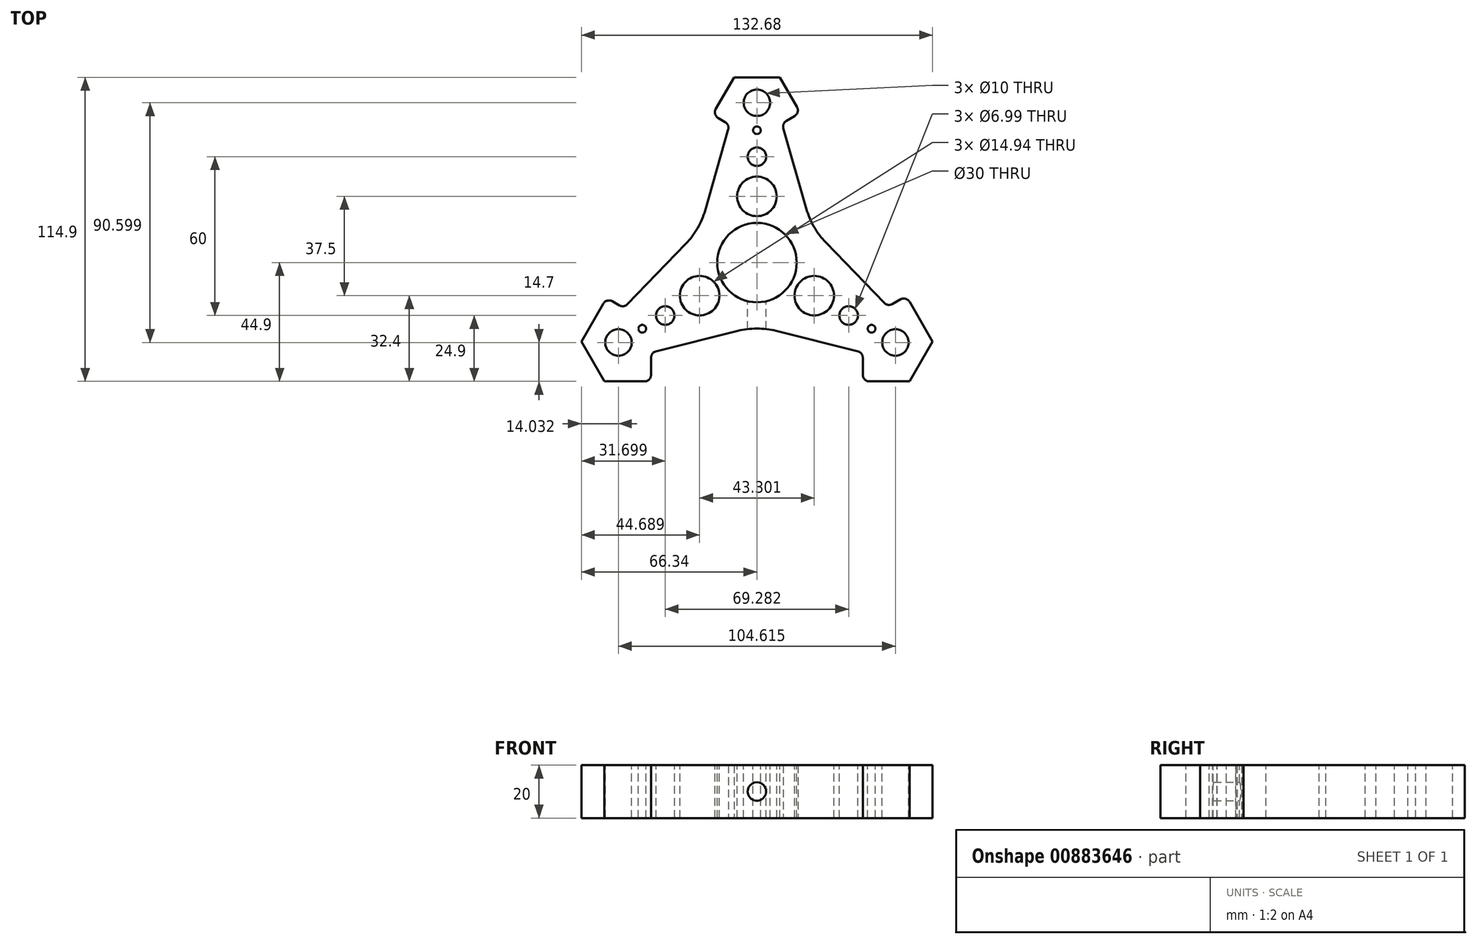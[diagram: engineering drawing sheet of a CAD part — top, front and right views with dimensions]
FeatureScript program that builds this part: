
annotation { "Feature Type Name" : "Feature", "Feature Type Description" : "" }
export const myFeature = defineFeature(function(context is Context, id is Id, definition is map)
    precondition{}
    {
        {
            var Q0;
            Q0=qCreatedBy(makeId("Top.planeOp"),FACE);
            var sketch = newSketch(context, id + "F0", { "sketchPlane" : qUnion([Q0])});
            skLineSegment(sketch, "E0", {"start": v(0, 0) * mm, "end": v(0, 85) * mm});
            skLineSegment(sketch, "E1", {"start": v(0, 85) * mm, "end": v(75, -44.9) * mm});
            skLineSegment(sketch, "E2", {"start": v(75, -44.9) * mm, "end": v(-75, -44.9) * mm});
            skLineSegment(sketch, "E3", {"start": v(-75, -44.9) * mm, "end": v(0, 85) * mm});
            skSolve(sketch);
        }
        {
            var Q0;
            Q0=makeQuery(id+"F0.imprint","IMPRINT",FACE,{"disambiguationData":[TD([[makeQuery(id+"F0.imprint","IMPRINT",EDGE,{"derivedFrom":sQuery(id+"F0.wireOp",EDGE,"E1")}),-1.0]])]});
            extrude(context, id + "F1", {"entities" : qUnion([Q0]), "depth" : 20 * mm, "offsetDistance" : 25 * mm});
        }
        {
            var Q0;
            Q0=makeQuery(id+"F1.opExtrude","SWEPT_EDGE",EDGE,{"disambiguationData":[OSD([sQuery(id+"F0.wireOp",EDGE,"E2"),sQuery(id+"F0.wireOp",EDGE,"E3")])]});
            var Q1;
            Q1=makeQuery(id+"F1.opExtrude","SWEPT_EDGE",EDGE,{"disambiguationData":[OSD([sQuery(id+"F0.wireOp",EDGE,"E1"),sQuery(id+"F0.wireOp",EDGE,"E2")])]});
            var Q2;
            Q2=makeQuery(id+"F1.opExtrude","SWEPT_EDGE",EDGE,{"disambiguationData":[OSD([sQuery(id+"F0.wireOp",EDGE,"E1"),sQuery(id+"F0.wireOp",EDGE,"E3")])]});
            chamfer(context, id + "F2", {"entities" : qUnion([Q0, Q1, Q2]), "width" : 10 * mm, "tangentPropagation" : true});
        }
        {
            var Q0;
            Q0=makeQuery(id+"F1.opExtrude","CAP_FACE",FACE,{"disambiguationData":[OSD([sQuery(id+"F0.wireOp",EDGE,"E1"),sQuery(id+"F0.wireOp",EDGE,"E2"),sQuery(id+"F0.wireOp",EDGE,"E3")])],"isStart":false});
            var sketch = newSketch(context, id + "F3", { "sketchPlane" : qUnion([Q0])});
            skCircle(sketch, "E4", {"center": v(0, 60.4) * mm, "radius": 3.81 * mm});
            skCircle(sketch, "E5.1.0", {"center": v(-52.3, -30.2) * mm, "radius": 3.81 * mm});
            skCircle(sketch, "E5.2.0", {"center": v(52.3, -30.2) * mm, "radius": 3.81 * mm});
            skPoint(sketch, "E5.center", {"position": v(0, 0) * mm});
            skSolve(sketch);
        }
        {
            var Q0;
            Q0=sQuery(id+"F3.wireOp",VERTEX,"E4.center");
            var Q1;
            Q1=sQuery(id+"F3.wireOp",VERTEX,"E5.2.0.center");
            var Q2;
            Q2=sQuery(id+"F3.wireOp",VERTEX,"E5.1.0.center");
            var Q3;
            Q3=makeQuery(id+"F1.opExtrude","SWEPT_BODY",BODY,{"disambiguationData":[OSD([sQuery(id+"F0.wireOp",EDGE,"E1"),sQuery(id+"F0.wireOp",EDGE,"E2"),sQuery(id+"F0.wireOp",EDGE,"E3")])]});
            hole(context, id + "F4", {"style" : HoleStyle.SIMPLE, "endStyle" : HoleEndStyle.BLIND, "holeDiameter" : 10 * mm, "majorDiameter" : 5 * mm, "holeDepth" : 100 * mm, "isTappedThrough" : true, "tappedDepth" : 12 * mm, "tapClearance" : 3, "locations" : qUnion([Q0, Q1, Q2]), "scope" : qUnion([Q3])});
        }
        {
            var Q0;
            Q0=makeQuery(id+"F1.opExtrude","CAP_FACE",FACE,{"disambiguationData":[OSD([sQuery(id+"F0.wireOp",EDGE,"E1"),sQuery(id+"F0.wireOp",EDGE,"E2"),sQuery(id+"F0.wireOp",EDGE,"E3")])],"isStart":false});
            var sketch = newSketch(context, id + "F5", { "sketchPlane" : qUnion([Q0])});
            skSolve(sketch);
        }
        {
            var Q0;
            {var subQ0=sQuery(id+"F0.wireOp",EDGE,"E1");Q0=makeQuery(id+"F5.imprint","IMPRINT",FACE,{"disambiguationData":[TD([[makeQuery(id+"F5.imprint","IMPRINT",EDGE,{"derivedFrom":makeQuery(id+"F1.opExtrude","CAP_EDGE",EDGE,{"disambiguationData":[OSD([subQ0])],"isStart":false})}),-1.0]])]});}
            var sketch = newSketch(context, id + "F6", { "sketchPlane" : qUnion([Q0])});
            skCircle(sketch, "E6", {"center": v(0, 0) * mm, "radius": 12.1 * mm});
            skSolve(sketch);
        }
        {
            var Q0;
            Q0=sQuery(id+"F6.wireOp",VERTEX,"E6.center");
            var Q1;
            Q1=makeQuery(id+"F1.opExtrude","SWEPT_BODY",BODY,{"disambiguationData":[OSD([sQuery(id+"F0.wireOp",EDGE,"E1"),sQuery(id+"F0.wireOp",EDGE,"E2"),sQuery(id+"F0.wireOp",EDGE,"E3")])]});
            hole(context, id + "F7", {"style" : HoleStyle.SIMPLE, "endStyle" : HoleEndStyle.BLIND, "holeDiameter" : 30 * mm, "majorDiameter" : 5 * mm, "holeDepth" : 100 * mm, "isTappedThrough" : true, "tappedDepth" : 12 * mm, "tapClearance" : 3, "locations" : qUnion([Q0]), "scope" : qUnion([Q1])});
        }
        {
            var Q0;
            {var subQ0=sQuery(id+"F0.wireOp",EDGE,"E1");Q0=makeQuery(id+"F5.imprint","IMPRINT",FACE,{"disambiguationData":[TD([[makeQuery(id+"F5.imprint","IMPRINT",EDGE,{"derivedFrom":makeQuery(id+"F1.opExtrude","CAP_EDGE",EDGE,{"disambiguationData":[OSD([subQ0])],"isStart":false})}),-1.0]])]});}
            var sketch = newSketch(context, id + "F8", { "sketchPlane" : qUnion([Q0])});
            skLineSegment(sketch, "E7", {"start": v(0, 0) * mm, "end": v(0, -48) * mm});
            skLineSegment(sketch, "E8", {"start": v(0, -48) * mm, "end": v(40, -48) * mm});
            skLineSegment(sketch, "E9", {"start": v(40, -48) * mm, "end": v(40, -34) * mm});
            skLineSegment(sketch, "E10", {"start": v(40, -34) * mm, "end": v(0, -24) * mm});
            skLineSegment(sketch, "E11", {"start": v(0, -24) * mm, "end": v(0, -48) * mm});
            skLineSegment(sketch, "E12.MirrorCS", {"start": v(-40, -34) * mm, "end": v(0, -24) * mm});
            skLineSegment(sketch, "E13.MirrorCS", {"start": v(-40, -48) * mm, "end": v(-40, -34) * mm});
            skLineSegment(sketch, "E14.MirrorCS", {"start": v(0, -48) * mm, "end": v(-40, -48) * mm});
            skLineSegment(sketch, "E15.1.0", {"start": v(61.57, -9.64) * mm, "end": v(49.44, -16.64) * mm});
            skLineSegment(sketch, "E15.1.1", {"start": v(20.78, 13) * mm, "end": v(41.57, 25) * mm});
            skLineSegment(sketch, "E15.1.2", {"start": v(41.57, 25) * mm, "end": v(61.57, -9.64) * mm});
            skLineSegment(sketch, "E15.1.3", {"start": v(41.57, 25) * mm, "end": v(21.57, 59.64) * mm});
            skLineSegment(sketch, "E15.1.4", {"start": v(49.44, -16.64) * mm, "end": v(20.78, 13) * mm});
            skLineSegment(sketch, "E15.1.5", {"start": v(9.44, 52.64) * mm, "end": v(20.78, 13) * mm});
            skLineSegment(sketch, "E15.1.6", {"start": v(21.57, 59.64) * mm, "end": v(9.44, 52.64) * mm});
            skLineSegment(sketch, "E15.2.0", {"start": v(-22.44, 59.14) * mm, "end": v(-10.31, 52.14) * mm});
            skLineSegment(sketch, "E15.2.1", {"start": v(-21.65, 12.5) * mm, "end": v(-42.44, 24.5) * mm});
            skLineSegment(sketch, "E15.2.2", {"start": v(-42.44, 24.5) * mm, "end": v(-22.44, 59.14) * mm});
            skLineSegment(sketch, "E15.2.3", {"start": v(-42.44, 24.5) * mm, "end": v(-62.44, -10.14) * mm});
            skLineSegment(sketch, "E15.2.4", {"start": v(-10.31, 52.14) * mm, "end": v(-21.65, 12.5) * mm});
            skLineSegment(sketch, "E15.2.5", {"start": v(-50.31, -17.14) * mm, "end": v(-21.65, 12.5) * mm});
            skLineSegment(sketch, "E15.2.6", {"start": v(-62.44, -10.14) * mm, "end": v(-50.31, -17.14) * mm});
            skPoint(sketch, "E15.center", {"position": v(-0.29, 0.5) * mm});
            skSolve(sketch);
        }
        {
            var Q0;
            Q0 = qSketchRegion(id + "F8", true);
            extrude(context, id + "F9", {"entities" : qUnion([Q0]), "operationType" : NewBodyOperationType.REMOVE, "oppositeDirection" : true, "depth" : 25 * mm, "offsetDistance" : 25 * mm});
        }
        {
            var Q0;
            Q0=makeQuery(id+"F9.boolean.opBoolean","COPY",EDGE,{"derivedFrom":makeQuery(id+"F9.opExtrude","SWEPT_EDGE",EDGE,{"disambiguationData":[OSD([sQuery(id+"F8.wireOp",EDGE,"E12.MirrorCS"),sQuery(id+"F8.wireOp",EDGE,"E13.MirrorCS")])]})});
            var Q1;
            Q1=makeQuery(id+"F9.boolean.opBoolean","COPY",EDGE,{"derivedFrom":makeQuery(id+"F9.opExtrude","SWEPT_EDGE",EDGE,{"disambiguationData":[OSD([sQuery(id+"F8.wireOp",EDGE,"E15.2.5"),sQuery(id+"F8.wireOp",EDGE,"E15.2.6")])]})});
            var Q2;
            Q2=makeQuery(id+"F9.boolean.opBoolean","COPY",EDGE,{"derivedFrom":makeQuery(id+"F9.opExtrude","SWEPT_EDGE",EDGE,{"disambiguationData":[OSD([sQuery(id+"F8.wireOp",EDGE,"E15.2.0"),sQuery(id+"F8.wireOp",EDGE,"E15.2.4")])]})});
            var Q3;
            Q3=makeQuery(id+"F9.boolean.opBoolean","COPY",EDGE,{"derivedFrom":makeQuery(id+"F9.opExtrude","SWEPT_EDGE",EDGE,{"disambiguationData":[OSD([sQuery(id+"F8.wireOp",EDGE,"E15.1.5"),sQuery(id+"F8.wireOp",EDGE,"E15.1.6")])]})});
            var Q4;
            Q4=makeQuery(id+"F9.boolean.opBoolean","COPY",EDGE,{"derivedFrom":makeQuery(id+"F9.opExtrude","SWEPT_EDGE",EDGE,{"disambiguationData":[OSD([sQuery(id+"F8.wireOp",EDGE,"E15.1.0"),sQuery(id+"F8.wireOp",EDGE,"E15.1.4")])]})});
            var Q5;
            Q5=makeQuery(id+"F9.boolean.opBoolean","COPY",EDGE,{"derivedFrom":makeQuery(id+"F9.opExtrude","SWEPT_EDGE",EDGE,{"disambiguationData":[OSD([sQuery(id+"F8.wireOp",EDGE,"E9"),sQuery(id+"F8.wireOp",EDGE,"E10")])]})});
            var Q6;
            Q6=makeQuery(id+"F9.boolean.opBoolean","INTERSECT",EDGE,{"derivedFrom":[makeQuery(id+"F1.opExtrude","SWEPT_FACE",FACE,{"disambiguationData":[OSD([sQuery(id+"F0.wireOp",EDGE,"E2")])]}),makeQuery(id+"F9.opExtrude","SWEPT_FACE",FACE,{"disambiguationData":[OSD([sQuery(id+"F8.wireOp",EDGE,"E9")])]})]});
            var Q7;
            Q7=makeQuery(id+"F9.boolean.opBoolean","INTERSECT",EDGE,{"derivedFrom":[makeQuery(id+"F1.opExtrude","SWEPT_FACE",FACE,{"disambiguationData":[OSD([sQuery(id+"F0.wireOp",EDGE,"E1")])]}),makeQuery(id+"F9.opExtrude","SWEPT_FACE",FACE,{"disambiguationData":[OSD([sQuery(id+"F8.wireOp",EDGE,"E15.1.0")])]})]});
            var Q8;
            Q8=makeQuery(id+"F9.boolean.opBoolean","INTERSECT",EDGE,{"derivedFrom":[makeQuery(id+"F1.opExtrude","SWEPT_FACE",FACE,{"disambiguationData":[OSD([sQuery(id+"F0.wireOp",EDGE,"E1")])]}),makeQuery(id+"F9.opExtrude","SWEPT_FACE",FACE,{"disambiguationData":[OSD([sQuery(id+"F8.wireOp",EDGE,"E15.1.6")])]})]});
            var Q9;
            Q9=makeQuery(id+"F9.boolean.opBoolean","INTERSECT",EDGE,{"derivedFrom":[makeQuery(id+"F1.opExtrude","SWEPT_FACE",FACE,{"disambiguationData":[OSD([sQuery(id+"F0.wireOp",EDGE,"E3")])]}),makeQuery(id+"F9.opExtrude","SWEPT_FACE",FACE,{"disambiguationData":[OSD([sQuery(id+"F8.wireOp",EDGE,"E15.2.0")])]})]});
            var Q10;
            Q10=makeQuery(id+"F9.boolean.opBoolean","INTERSECT",EDGE,{"derivedFrom":[makeQuery(id+"F1.opExtrude","SWEPT_FACE",FACE,{"disambiguationData":[OSD([sQuery(id+"F0.wireOp",EDGE,"E3")])]}),makeQuery(id+"F9.opExtrude","SWEPT_FACE",FACE,{"disambiguationData":[OSD([sQuery(id+"F8.wireOp",EDGE,"E15.2.6")])]})]});
            var Q11;
            Q11=makeQuery(id+"F9.boolean.opBoolean","INTERSECT",EDGE,{"derivedFrom":[makeQuery(id+"F1.opExtrude","SWEPT_FACE",FACE,{"disambiguationData":[OSD([sQuery(id+"F0.wireOp",EDGE,"E2")])]}),makeQuery(id+"F9.opExtrude","SWEPT_FACE",FACE,{"disambiguationData":[OSD([sQuery(id+"F8.wireOp",EDGE,"E13.MirrorCS")])]})]});
            fillet(context, id + "F10", {"entities" : qUnion([Q0, Q1, Q2, Q3, Q4, Q5, Q6, Q7, Q8, Q9, Q10, Q11]), "radius" : 2.5 * mm, "tangentPropagation" : true, "allowEdgeOverflow" : false});
        }
        {
            var Q0;
            Q0=makeQuery(id+"F9.boolean.opBoolean","COPY",EDGE,{"derivedFrom":makeQuery(id+"F9.opExtrude","SWEPT_EDGE",EDGE,{"disambiguationData":[OSD([sQuery(id+"F8.wireOp",EDGE,"E10"),sQuery(id+"F8.wireOp",EDGE,"E12.MirrorCS"),sQuery(id+"F8.wireOp",EDGE,"E7")])]})});
            var Q1;
            Q1=makeQuery(id+"F9.boolean.opBoolean","COPY",EDGE,{"derivedFrom":makeQuery(id+"F9.opExtrude","SWEPT_EDGE",EDGE,{"disambiguationData":[OSD([sQuery(id+"F8.wireOp",EDGE,"E15.1.1"),sQuery(id+"F8.wireOp",EDGE,"E15.1.4"),sQuery(id+"F8.wireOp",EDGE,"E15.1.5")])]})});
            var Q2;
            Q2=makeQuery(id+"F9.boolean.opBoolean","COPY",EDGE,{"derivedFrom":makeQuery(id+"F9.opExtrude","SWEPT_EDGE",EDGE,{"disambiguationData":[OSD([sQuery(id+"F8.wireOp",EDGE,"E15.2.1"),sQuery(id+"F8.wireOp",EDGE,"E15.2.4"),sQuery(id+"F8.wireOp",EDGE,"E15.2.5")])]})});
            fillet(context, id + "F11", {"entities" : qUnion([Q0, Q1, Q2]), "radius" : 30 * mm, "tangentPropagation" : true, "allowEdgeOverflow" : false});
        }
        {
            var Q0;
            {var subQ0=sQuery(id+"F0.wireOp",EDGE,"E1");Q0=makeQuery(id+"F5.imprint","IMPRINT",FACE,{"disambiguationData":[TD([[makeQuery(id+"F5.imprint","IMPRINT",EDGE,{"derivedFrom":makeQuery(id+"F1.opExtrude","CAP_EDGE",EDGE,{"disambiguationData":[OSD([subQ0])],"isStart":false})}),-1.0]])]});}
            var sketch = newSketch(context, id + "F12", { "sketchPlane" : qUnion([Q0])});
            skCircle(sketch, "E16", {"center": v(0, 50) * mm, "radius": 1.45 * mm});
            skCircle(sketch, "E17", {"center": v(0, 40) * mm, "radius": 3.5 * mm});
            skCircle(sketch, "E18", {"center": v(0, 25) * mm, "radius": 7.47 * mm});
            skCircle(sketch, "E19.1.0", {"center": v(-34.64, -20) * mm, "radius": 3.5 * mm});
            skCircle(sketch, "E19.1.1", {"center": v(-21.65, -12.5) * mm, "radius": 7.47 * mm});
            skCircle(sketch, "E19.1.2", {"center": v(-43.3, -25) * mm, "radius": 1.45 * mm});
            skCircle(sketch, "E19.2.0", {"center": v(34.64, -20) * mm, "radius": 3.5 * mm});
            skCircle(sketch, "E19.2.1", {"center": v(21.65, -12.5) * mm, "radius": 7.47 * mm});
            skCircle(sketch, "E19.2.2", {"center": v(43.3, -25) * mm, "radius": 1.45 * mm});
            skPoint(sketch, "E19.center", {"position": v(0, 0) * mm});
            skSolve(sketch);
        }
        {
            var Q0;
            Q0 = qSketchRegion(id + "F12", true);
            extrude(context, id + "F13", {"entities" : qUnion([Q0]), "operationType" : NewBodyOperationType.REMOVE, "oppositeDirection" : true, "depth" : 25 * mm, "offsetDistance" : 25 * mm});
        }
        {
            var Q0;
            Q0=qCreatedBy(makeId("Front.planeOp"),FACE);
            var sketch = newSketch(context, id + "F14", { "sketchPlane" : qUnion([Q0])});
            skCircle(sketch, "E20", {"center": v(0, 10.05) * mm, "radius": 4.47 * mm});
            skSolve(sketch);
        }
        {
            var Q0;
            Q0=sQuery(id+"F14.wireOp",VERTEX,"E20.center");
            var Q1;
            Q1=makeQuery(id+"F1.opExtrude","SWEPT_BODY",BODY,{"disambiguationData":[OSD([sQuery(id+"F0.wireOp",EDGE,"E1"),sQuery(id+"F0.wireOp",EDGE,"E2"),sQuery(id+"F0.wireOp",EDGE,"E3")])]});
            hole(context, id + "F15", {"style" : HoleStyle.SIMPLE, "endStyle" : HoleEndStyle.BLIND, "oppositeDirection" : true, "holeDiameter" : 7 * mm, "majorDiameter" : 5 * mm, "holeDepth" : 100 * mm, "isTappedThrough" : true, "tappedDepth" : 12 * mm, "tapClearance" : 3, "locations" : qUnion([Q0]), "scope" : qUnion([Q1])});
        }
    });
